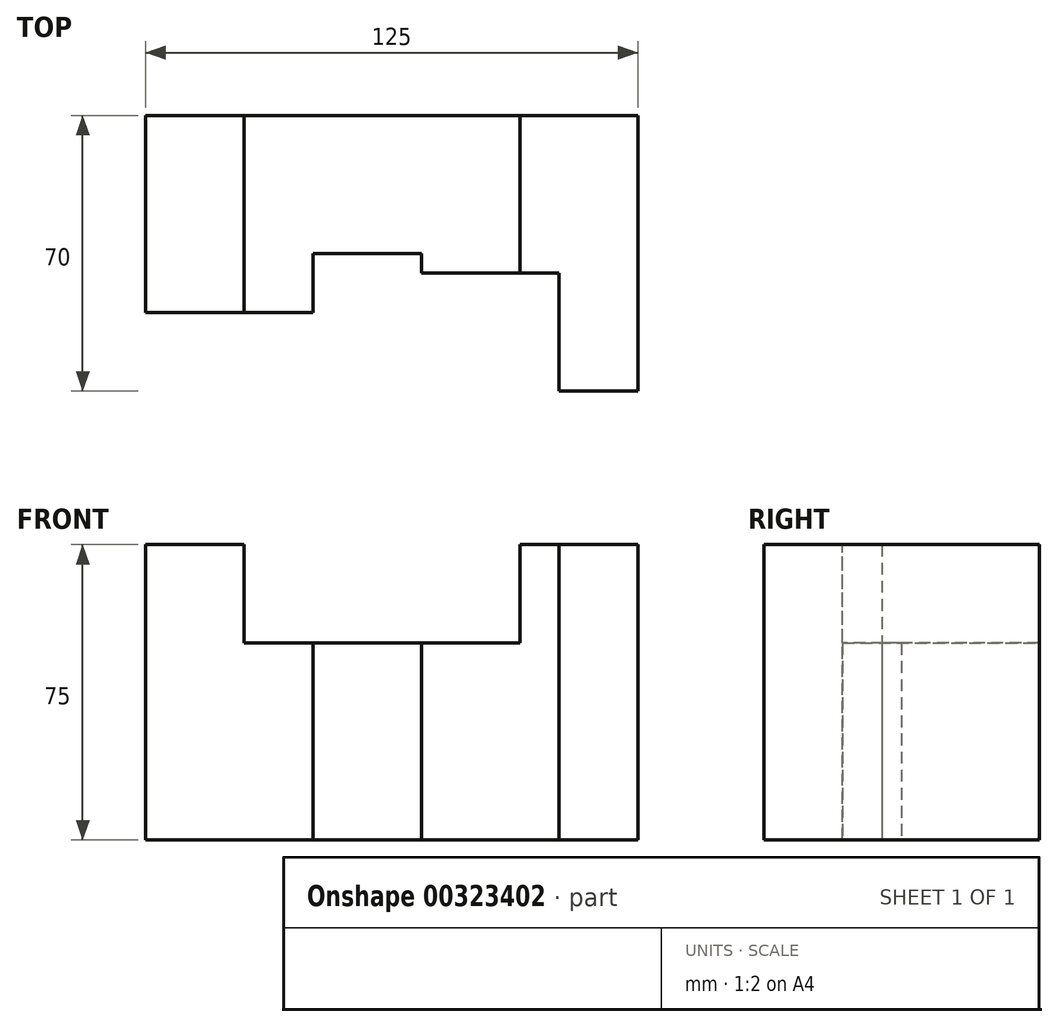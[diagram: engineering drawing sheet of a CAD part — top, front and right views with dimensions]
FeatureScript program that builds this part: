
annotation { "Feature Type Name" : "Feature", "Feature Type Description" : "" }
export const myFeature = defineFeature(function(context is Context, id is Id, definition is map)
    precondition{}
    {
        {
            var Q0;
            Q0=qCreatedBy(makeId("Front.planeOp"),FACE);
            var sketch = newSketch(context, id + "F0", { "sketchPlane" : qUnion([Q0])});
            skLineSegment(sketch, "E0.bottom", {"start": v(0, 0) * mm, "end": v(25, 0) * mm});
            skLineSegment(sketch, "E0.top", {"start": v(0, 75) * mm, "end": v(25, 75) * mm});
            skLineSegment(sketch, "E0.left", {"start": v(0, 0) * mm, "end": v(0, 75) * mm});
            skLineSegment(sketch, "E0.right", {"start": v(25, 0) * mm, "end": v(25, 75) * mm});
            skSolve(sketch);
        }
        {
            var Q0;
            Q0 = qSketchRegion(id + "F0", true);
            extrude(context, id + "F1", {"entities" : qUnion([Q0]), "depth" : 50 * mm});
        }
        {
            var Q0;
            Q0=makeQuery(id+"F1.opExtrude","SWEPT_FACE",FACE,{"disambiguationData":[OSD([sQuery(id+"F0.wireOp",EDGE,"E0.bottom")])]});
            var sketch = newSketch(context, id + "F2", { "sketchPlane" : qUnion([Q0])});
            skLineSegment(sketch, "E1.bottom", {"start": v(25, 0) * mm, "end": v(42.5, 0) * mm});
            skLineSegment(sketch, "E1.top", {"start": v(25, 50) * mm, "end": v(42.5, 50) * mm});
            skLineSegment(sketch, "E1.left", {"start": v(25, 0) * mm, "end": v(25, 50) * mm});
            skLineSegment(sketch, "E1.right", {"start": v(42.5, 0) * mm, "end": v(42.5, 50) * mm});
            skLineSegment(sketch, "E2", {"start": v(42.5, 0) * mm, "end": v(42.5, 35) * mm});
            skLineSegment(sketch, "E3", {"start": v(42.5, 35) * mm, "end": v(70, 35) * mm});
            skLineSegment(sketch, "E4", {"start": v(70, 35) * mm, "end": v(70, 0) * mm});
            skLineSegment(sketch, "E5", {"start": v(70, 0) * mm, "end": v(42.5, 0) * mm});
            skLineSegment(sketch, "E6.bottom", {"start": v(70, 0) * mm, "end": v(95, 0) * mm});
            skLineSegment(sketch, "E6.top", {"start": v(70, 40) * mm, "end": v(95, 40) * mm});
            skLineSegment(sketch, "E6.left", {"start": v(70, 0) * mm, "end": v(70, 40) * mm});
            skLineSegment(sketch, "E6.right", {"start": v(95, 0) * mm, "end": v(95, 40) * mm});
            skSolve(sketch);
        }
        {
            var Q0;
            Q0 = qSketchRegion(id + "F2", true);
            extrude(context, id + "F3", {"entities" : qUnion([Q0]), "operationType" : NewBodyOperationType.ADD, "oppositeDirection" : true, "depth" : 50 * mm});
        }
        {
            var Q0;
            Q0=makeQuery(id+"F3.boolean.opBoolean","MERGE",FACE,{"derivedFrom":[makeQuery(id+"F1.opExtrude","SWEPT_FACE",FACE,{"disambiguationData":[OSD([sQuery(id+"F0.wireOp",EDGE,"E0.bottom")])]}),makeQuery(id+"F3.opExtrude","CAP_FACE",FACE,{"disambiguationData":[OSD([sQuery(id+"F2.wireOp",EDGE,"E1.bottom"),sQuery(id+"F2.wireOp",EDGE,"E1.top"),sQuery(id+"F2.wireOp",EDGE,"E1.left"),sQuery(id+"F2.wireOp",EDGE,"E1.right"),sQuery(id+"F2.wireOp",EDGE,"E3"),sQuery(id+"F2.wireOp",EDGE,"E5"),sQuery(id+"F2.wireOp",EDGE,"E6.bottom"),sQuery(id+"F2.wireOp",EDGE,"E6.top"),sQuery(id+"F2.wireOp",EDGE,"E6.left"),sQuery(id+"F2.wireOp",EDGE,"E6.right")])],"isStart":true})]});
            var sketch = newSketch(context, id + "F4", { "sketchPlane" : qUnion([Q0])});
            skLineSegment(sketch, "E7.bottom", {"start": v(95, 0) * mm, "end": v(105, 0) * mm});
            skLineSegment(sketch, "E7.top", {"start": v(95, 40) * mm, "end": v(105, 40) * mm});
            skLineSegment(sketch, "E7.left", {"start": v(95, 0) * mm, "end": v(95, 40) * mm});
            skLineSegment(sketch, "E7.right", {"start": v(105, 0) * mm, "end": v(105, 40) * mm});
            skLineSegment(sketch, "E8.bottom", {"start": v(105, 0) * mm, "end": v(125, 0) * mm});
            skLineSegment(sketch, "E8.top", {"start": v(105, 70) * mm, "end": v(125, 70) * mm});
            skLineSegment(sketch, "E8.left", {"start": v(105, 0) * mm, "end": v(105, 70) * mm});
            skLineSegment(sketch, "E8.right", {"start": v(125, 0) * mm, "end": v(125, 70) * mm});
            skSolve(sketch);
        }
        {
            var Q0;
            Q0 = qSketchRegion(id + "F4", true);
            extrude(context, id + "F5", {"entities" : qUnion([Q0]), "operationType" : NewBodyOperationType.ADD, "oppositeDirection" : true, "depth" : 75 * mm});
        }
    });
